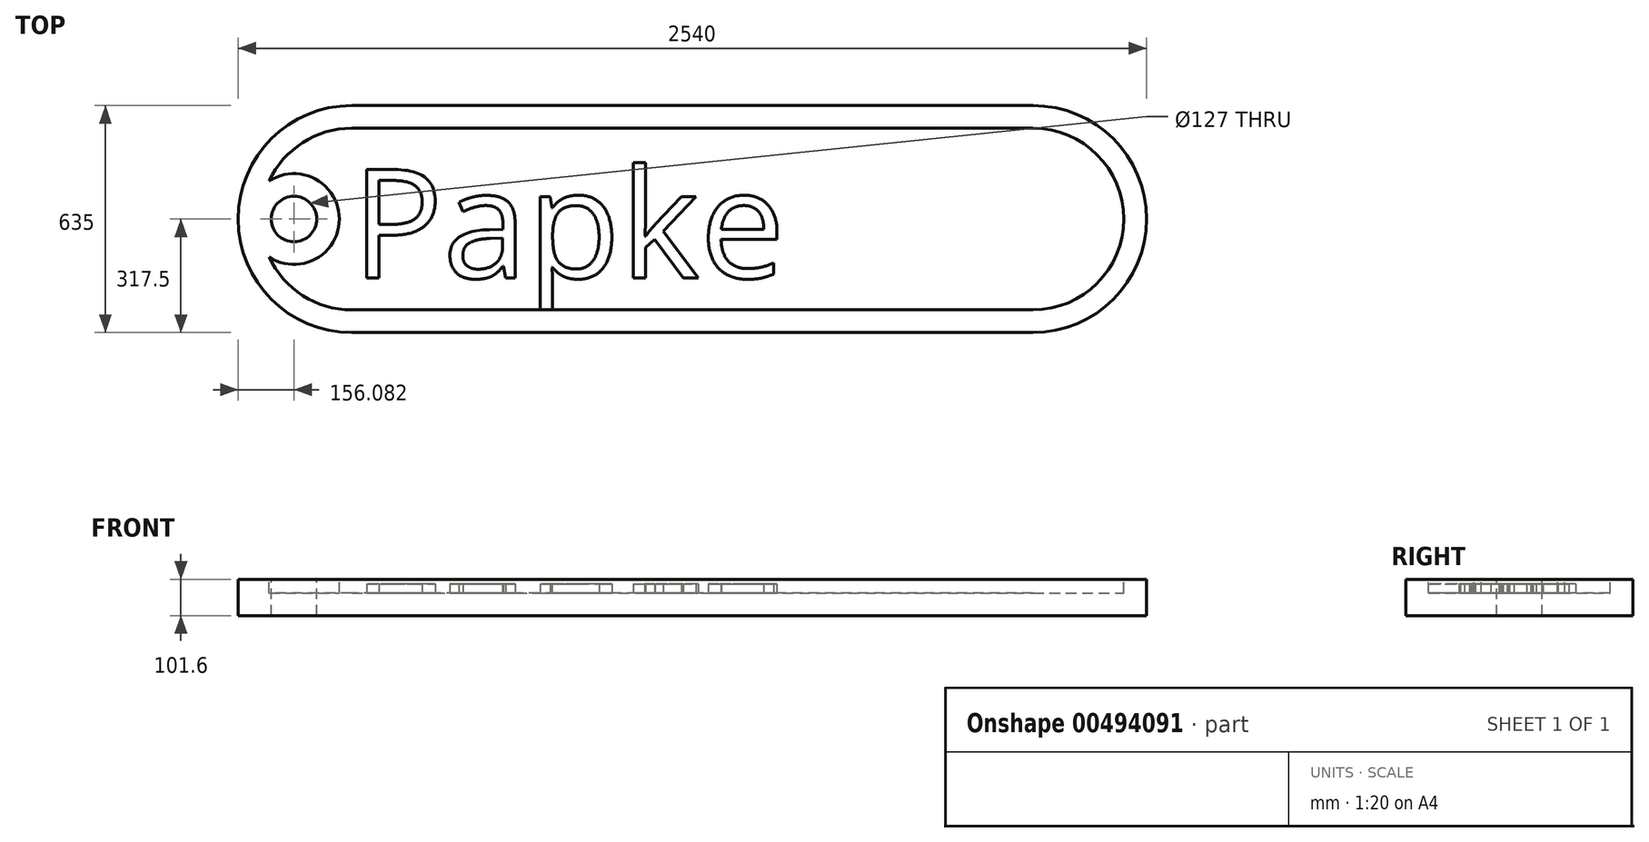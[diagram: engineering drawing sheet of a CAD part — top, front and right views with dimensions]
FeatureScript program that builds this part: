
annotation { "Feature Type Name" : "Feature", "Feature Type Description" : "" }
export const myFeature = defineFeature(function(context is Context, id is Id, definition is map)
    precondition{}
    {
        {
            var Q0;
            Q0=qCreatedBy(makeId("Top.planeOp"),FACE);
            var sketch = newSketch(context, id + "F0", { "sketchPlane" : qUnion([Q0])});
            skLineSegment(sketch, "E0.bottom", {"start": v(0, 0) * mm, "end": v(1905, 0) * mm});
            skLineSegment(sketch, "E0.top", {"start": v(0, 635) * mm, "end": v(1905, 635) * mm});
            skArc(sketch, "E1", {"start": v(1905, 0) * mm, "mid": v(2222.5, 317.5) * mm, "end": v(1905, 635) * mm});
            skArc(sketch, "E2", {"start": v(0, 635) * mm, "mid": v(-317.5, 317.5) * mm, "end": v(0, 0) * mm});
            skSolve(sketch);
        }
        {
            var Q0;
            Q0=makeQuery(id+"F0.imprint","IMPRINT",FACE,{"disambiguationData":[TD([[makeQuery(id+"F0.imprint","IMPRINT",EDGE,{"derivedFrom":sQuery(id+"F0.wireOp",EDGE,"E0.bottom")}),1.0]])]});
            extrude(context, id + "F1", {"entities" : qUnion([Q0]), "depth" : 101.6 * mm});
        }
        {
            var Q0;
            Q0=makeQuery(id+"F1.opExtrude","CAP_FACE",FACE,{"disambiguationData":[OSD([sQuery(id+"F0.wireOp",EDGE,"E0.bottom"),sQuery(id+"F0.wireOp",EDGE,"E0.top"),sQuery(id+"F0.wireOp",EDGE,"E1"),sQuery(id+"F0.wireOp",EDGE,"E2")])],"isStart":false});
            var sketch = newSketch(context, id + "F2", { "sketchPlane" : qUnion([Q0])});
            skArc(sketch, "E3", {"start": v(0, 571.5) * mm, "mid": v(-136.86, 531.47) * mm, "end": v(-230.59, 424) * mm});
            skArc(sketch, "E4", {"start": v(1905, 63.5) * mm, "mid": v(2159, 317.5) * mm, "end": v(1905, 571.5) * mm});
            skLineSegment(sketch, "E5", {"start": v(0, 63.5) * mm, "end": v(1905, 63.5) * mm});
            skLineSegment(sketch, "E6", {"start": v(1905, 571.5) * mm, "end": v(0, 571.5) * mm});
            skLineSegment(sketch, "E7", {"start": v(-330.68, 763.17) * mm, "end": v(-330.68, -76.28) * mm});
            skArc(sketch, "E8", {"start": v(-230.59, 211) * mm, "mid": v(-34.42, 317.5) * mm, "end": v(-230.59, 424) * mm});
            skArc(sketch, "E9.trimOffspring", {"start": v(-230.59, 211) * mm, "mid": v(-136.86, 103.53) * mm, "end": v(0, 63.5) * mm});
            skSolve(sketch);
        }
        {
            var Q0;
            Q0=makeQuery(id+"F2.imprint","IMPRINT",FACE,{"disambiguationData":[TD([[makeQuery(id+"F2.imprint","IMPRINT",EDGE,{"derivedFrom":sQuery(id+"F2.wireOp",EDGE,"E3")}),1.0]])]});
            extrude(context, id + "F3", {"entities" : qUnion([Q0]), "operationType" : NewBodyOperationType.REMOVE, "oppositeDirection" : true, "depth" : 38.1 * mm});
        }
        {
            var Q0;
            Q0=makeQuery(id+"F1.opExtrude","CAP_FACE",FACE,{"disambiguationData":[OSD([sQuery(id+"F0.wireOp",EDGE,"E0.bottom"),sQuery(id+"F0.wireOp",EDGE,"E0.top"),sQuery(id+"F0.wireOp",EDGE,"E1"),sQuery(id+"F0.wireOp",EDGE,"E2")])],"isStart":false});
            var sketch = newSketch(context, id + "F4", { "sketchPlane" : qUnion([Q0])});
            skCircle(sketch, "E10", {"center": v(-161.42, 317.5) * mm, "radius": 63.5 * mm});
            skSolve(sketch);
        }
        {
            var Q0;
            Q0=makeQuery(id+"F4.imprint","IMPRINT",FACE,{"disambiguationData":[TD([[makeQuery(id+"F4.imprint","IMPRINT",EDGE,{"derivedFrom":sQuery(id+"F4.wireOp",EDGE,"E10")}),1.0]])]});
            extrude(context, id + "F5", {"entities" : qUnion([Q0]), "operationType" : NewBodyOperationType.REMOVE, "oppositeDirection" : true, "depth" : 101.6 * mm});
        }
        {
            var Q0;
            Q0=makeQuery(id+"F3.boolean.opBoolean","COPY",FACE,{"derivedFrom":makeQuery(id+"F3.opExtrude","CAP_FACE",FACE,{"disambiguationData":[OSD([sQuery(id+"F2.wireOp",EDGE,"E3"),sQuery(id+"F2.wireOp",EDGE,"E4"),sQuery(id+"F2.wireOp",EDGE,"E5"),sQuery(id+"F2.wireOp",EDGE,"E6"),sQuery(id+"F2.wireOp",EDGE,"E8"),sQuery(id+"F2.wireOp",EDGE,"E9.trimOffspring")])],"isStart":false})});
            var sketch = newSketch(context, id + "F6", { "sketchPlane" : qUnion([Q0])});
            skText(sketch, "E11", { "text": "Papke", "fontName": "OpenSans-Regular.ttf"});
            const initialGuessF6  = {"E11": [0, 0.15303, 1, 0, 0.30537]};
            skSetInitialGuess(sketch, initialGuessF6);
            skSolve(sketch);
        }
        {
            var Q0;
            Q0 = qSketchRegion(id + "F6", true);
            extrude(context, id + "F7", {"entities" : qUnion([Q0]), "operationType" : NewBodyOperationType.ADD, "depth" : 25.4 * mm});
        }
    });
